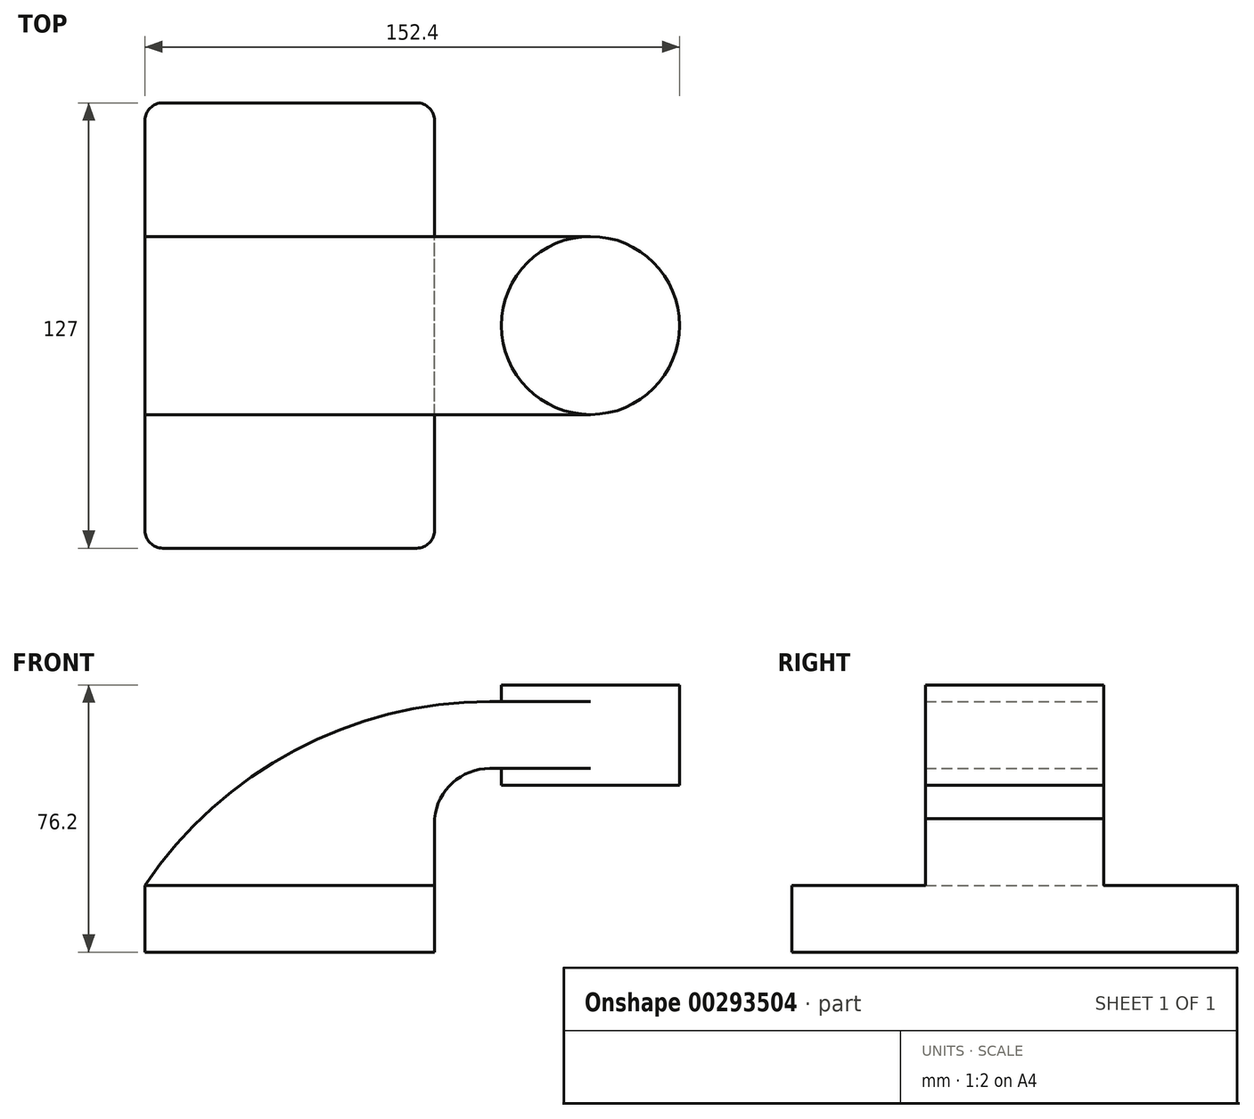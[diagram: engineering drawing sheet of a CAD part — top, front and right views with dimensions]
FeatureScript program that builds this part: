
annotation { "Feature Type Name" : "Feature", "Feature Type Description" : "" }
export const myFeature = defineFeature(function(context is Context, id is Id, definition is map)
    precondition{}
    {
        {
            var Q0;
            Q0=qCreatedBy(makeId("Front.planeOp"),FACE);
            var sketch = newSketch(context, id + "F0", { "sketchPlane" : qUnion([Q0])});
            skLineSegment(sketch, "E0.bottom", {"start": v(-31.27, -52.37) * mm, "end": v(51.28, -52.37) * mm});
            skLineSegment(sketch, "E0.top", {"start": v(-31.27, -71.42) * mm, "end": v(51.28, -71.42) * mm});
            skLineSegment(sketch, "E0.left", {"start": v(-31.27, -52.37) * mm, "end": v(-31.27, -71.42) * mm});
            skLineSegment(sketch, "E0.right", {"start": v(51.28, -52.37) * mm, "end": v(51.28, -71.42) * mm});
            skLineSegment(sketch, "E1.bottom", {"start": v(95.73, 0) * mm, "end": v(67.08, 0) * mm});
            skLineSegment(sketch, "E1.top", {"start": v(95.73, -19.02) * mm, "end": v(67.08, -19.02) * mm});
            skLineSegment(sketch, "E1.left", {"start": v(95.73, 0) * mm, "end": v(95.73, -19.02) * mm});
            skLineSegment(sketch, "E1.right", {"start": v(67.08, 0) * mm, "end": v(67.08, -19.02) * mm});
            skLineSegment(sketch, "E2.bottom", {"start": v(51.28, -52.37) * mm, "end": v(32.23, -52.37) * mm});
            skLineSegment(sketch, "E2.top", {"start": v(51.28, -33.32) * mm, "end": v(32.23, -33.32) * mm});
            skLineSegment(sketch, "E2.left", {"start": v(51.28, -52.37) * mm, "end": v(51.28, -33.32) * mm});
            skLineSegment(sketch, "E2.right", {"start": v(32.23, -52.37) * mm, "end": v(32.23, -33.32) * mm});
            skLineSegment(sketch, "E3.bottom", {"start": v(70.33, 4.78) * mm, "end": v(121.13, 4.78) * mm});
            skLineSegment(sketch, "E3.top", {"start": v(70.33, -23.8) * mm, "end": v(121.13, -23.8) * mm});
            skLineSegment(sketch, "E3.left", {"start": v(70.33, 4.78) * mm, "end": v(70.33, -23.8) * mm});
            skLineSegment(sketch, "E3.right", {"start": v(121.13, 4.78) * mm, "end": v(121.13, -23.8) * mm});
            skLineSegment(sketch, "E4", {"start": v(95.73, 4.78) * mm, "end": v(95.73, -23.8) * mm});
            skPoint(sketch, "E5", {"position": v(95.73, -9.51) * mm});
            skArc(sketch, "E6", {"start": v(67.08, 0) * mm, "mid": v(42.97, -9.67) * mm, "end": v(32.23, -33.32) * mm});
            skArc(sketch, "E7", {"start": v(67.08, 0) * mm, "mid": v(11.37, -13.9) * mm, "end": v(-31.27, -52.37) * mm});
            skArc(sketch, "E8", {"start": v(67.08, -19.02) * mm, "mid": v(56.43, -23.13) * mm, "end": v(51.28, -33.32) * mm});
            skSolve(sketch);
        }
        {
            var Q0;
            Q0=makeQuery(id+"F0.imprint","IMPRINT",FACE,{"disambiguationData":[TD([[makeQuery(id+"F0.imprint","IMPRINT",EDGE,{"derivedFrom":sQuery(id+"F0.wireOp",EDGE,"E0.bottom")}),-1.0]])]});
            extrude(context, id + "F1", {"entities" : qUnion([Q0]), "endBound" : BoundingType.SYMMETRIC, "depth" : 127 * mm});
        }
        {
            var Q0;
            Q0=makeQuery(id+"F0.imprint","IMPRINT",FACE,{"disambiguationData":[TD([[makeQuery(id+"F0.imprint","IMPRINT",EDGE,{"derivedFrom":sQuery(id+"F0.wireOp",EDGE,"E0.bottom")}),1.0]])]});
            var Q1;
            Q1=makeQuery(id+"F0.imprint","IMPRINT",FACE,{"disambiguationData":[TD([[makeQuery(id+"F0.imprint","IMPRINT",EDGE,{"derivedFrom":sQuery(id+"F0.wireOp",EDGE,"E1.right")}),-1.0]])]});
            var Q2;
            Q2=makeQuery(id+"F0.imprint","IMPRINT",FACE,{"disambiguationData":[TD([[makeQuery(id+"F0.imprint","IMPRINT",EDGE,{"derivedFrom":sQuery(id+"F0.wireOp",EDGE,"E2.bottom")}),-1.0]])]});
            var Q3;
            {var subQ0=sQuery(id+"F0.wireOp",EDGE,"E1.right");Q3=makeQuery(id+"F0.imprint","IMPRINT",FACE,{"disambiguationData":[TD([[makeQuery(id+"F0.imprint","IMPRINT",EDGE,{"derivedFrom":subQ0}),1.0]])]});}
            var Q4;
            {var subQ0=sQuery(id+"F0.wireOp",EDGE,"E4");var subQ1=sQuery(id+"F0.wireOp",EDGE,"E1.bottom");var subQ2=makeQuery(id+"F0.imprint","INTERSECT",VERTEX,{"derivedFrom":[subQ1,subQ0]});Q4=makeQuery(id+"F0.imprint","IMPRINT",FACE,{"disambiguationData":[TD([[makeQuery(id+"F0.imprint","IMPRINT",EDGE,{"disambiguationData":[TD([[subQ2,-1.0]])],"derivedFrom":subQ1}),1.0]])]});}
            extrude(context, id + "F2", {"entities" : qUnion([Q0, Q1, Q2, Q3, Q4]), "operationType" : NewBodyOperationType.ADD, "endBound" : BoundingType.SYMMETRIC, "depth" : 50.8 * mm});
        }
        {
            var Q0;
            {var subQ0=sQuery(id+"F0.wireOp",EDGE,"E3.right");Q0=makeQuery(id+"F0.imprint","IMPRINT",FACE,{"disambiguationData":[TD([[makeQuery(id+"F0.imprint","IMPRINT",EDGE,{"derivedFrom":subQ0}),-1.0]])]});}
            var Q1;
            Q1=sQuery(id+"F0.wireOp",EDGE,"E4");
            revolve(context, id + "F3", {"operationType" : NewBodyOperationType.ADD, "entities" : qUnion([Q0]), "axis" : qUnion([Q1]), "revolveType" : RevolveType.FULL});
        }
        {
            var Q0;
            Q0=makeQuery(id+"F1.opExtrude","CAP_EDGE",EDGE,{"disambiguationData":[OSD([sQuery(id+"F0.wireOp",EDGE,"E0.left")])],"isStart":false});
            var Q1;
            Q1=makeQuery(id+"F1.opExtrude","CAP_EDGE",EDGE,{"disambiguationData":[OSD([sQuery(id+"F0.wireOp",EDGE,"E0.right")])],"isStart":false});
            var Q2;
            Q2=makeQuery(id+"F1.opExtrude","CAP_EDGE",EDGE,{"disambiguationData":[OSD([sQuery(id+"F0.wireOp",EDGE,"E0.right")])],"isStart":true});
            var Q3;
            Q3=makeQuery(id+"F1.opExtrude","CAP_EDGE",EDGE,{"disambiguationData":[OSD([sQuery(id+"F0.wireOp",EDGE,"E0.left")])],"isStart":true});
            fillet(context, id + "F4", {"entities" : qUnion([Q0, Q1, Q2, Q3]), "radius" : 5.08 * mm, "tangentPropagation" : true, "allowEdgeOverflow" : false});
        }
    });
